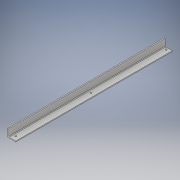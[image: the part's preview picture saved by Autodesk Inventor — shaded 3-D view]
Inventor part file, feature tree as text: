
AUTODESK INVENTOR PART (.ipt)
format: ipt  version: 2017 (Build 210142000, 142)  size: 118,784 bytes
history: native  units: in
note: dims shown in document units (in); Inventor stores cm internally (conversion verified against a paired STEP export)
features: sketch x3, hole x2, extrude x1
ambient origin geometry x8: Origin, YZ Plane, XZ Plane, XY Plane, X Axis, Y Axis, Z Axis, Center Point
bodies: Solid1 (feature_tree)
feature tree (6):
  extrude  "Extrusion1"  Depth=1.0in
  hole  "Hole1"  [1 undecoded]
  hole  "Hole2"  [1 undecoded]
  sketch  "Sketch1"  dims[d0=1.0in d1=1.0in]
  sketch  "Sketch2"  dims[d2=0.125in d3=19.5in d4=0.0in]
  sketch  "Sketch5"  dims[d5=0.5in d6=0.5in d7=0.7874in d9=18.75in d10=0.3937in d12=1.0in d14=0.201in d15=0.75in d16=0.385in d17=0.25in d18=0.5635in d19=1.0in d20=0.8108in d21=0.07in d24=0.201in d25=0.75in d26=0.385in d27=0.25in d28=0.5635in d29=1.0in d30=0.8108in]
note: 2 required parameter values undecoded (feature->parameter linkage not recoverable at this tier; creation-order binding heuristic only, values carry confidence <= 0.55)
